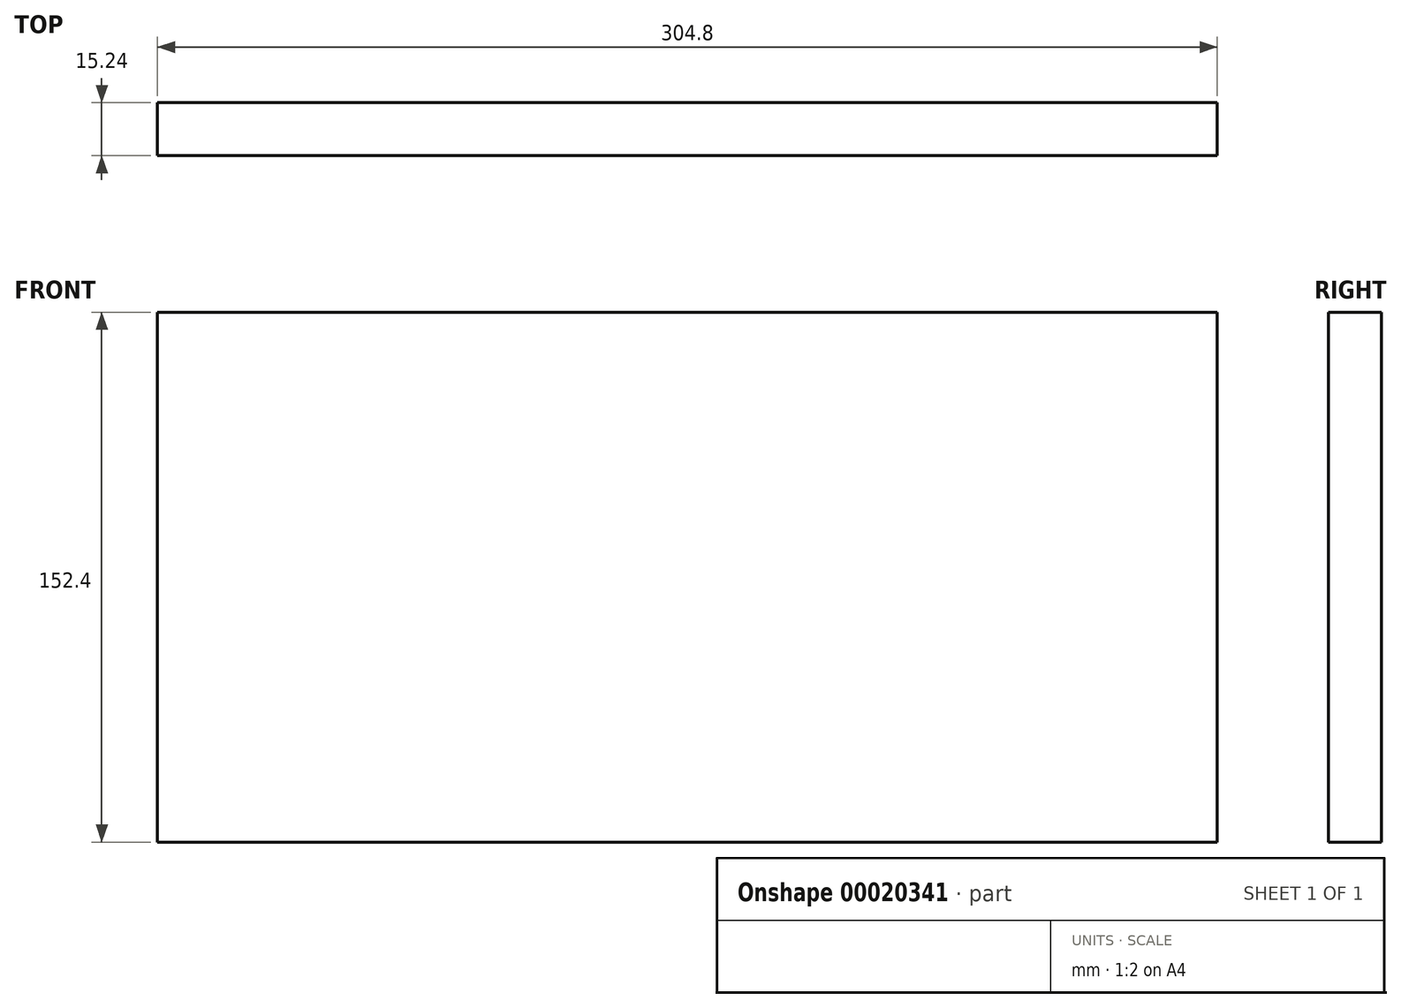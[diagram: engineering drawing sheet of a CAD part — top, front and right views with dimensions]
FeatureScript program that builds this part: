
annotation { "Feature Type Name" : "Feature", "Feature Type Description" : "" }
export const myFeature = defineFeature(function(context is Context, id is Id, definition is map)
    precondition{}
    {
        {
            var Q0;
            Q0=qCreatedBy(makeId("Front.planeOp"),FACE);
            var sketch = newSketch(context, id + "F0", { "sketchPlane" : qUnion([Q0])});
            skLineSegment(sketch, "E0.bottom", {"start": v(-54.88, 105.26) * mm, "end": v(249.92, 105.26) * mm});
            skLineSegment(sketch, "E0.top", {"start": v(-54.88, -47.14) * mm, "end": v(249.92, -47.14) * mm});
            skLineSegment(sketch, "E0.left", {"start": v(-54.88, 105.26) * mm, "end": v(-54.88, -47.14) * mm});
            skLineSegment(sketch, "E0.right", {"start": v(249.92, 105.26) * mm, "end": v(249.92, -47.14) * mm});
            skSolve(sketch);
        }
        {
            var Q0;
            Q0=makeQuery(id+"F0.imprint","IMPRINT",FACE,{"disambiguationData":[TD([[makeQuery(id+"F0.imprint","IMPRINT",EDGE,{"derivedFrom":sQuery(id+"F0.wireOp",EDGE,"E0.bottom")}),-1.0]])]});
            extrude(context, id + "F1", {"entities" : qUnion([Q0]), "depth" : 15.24 * mm});
        }
    });
